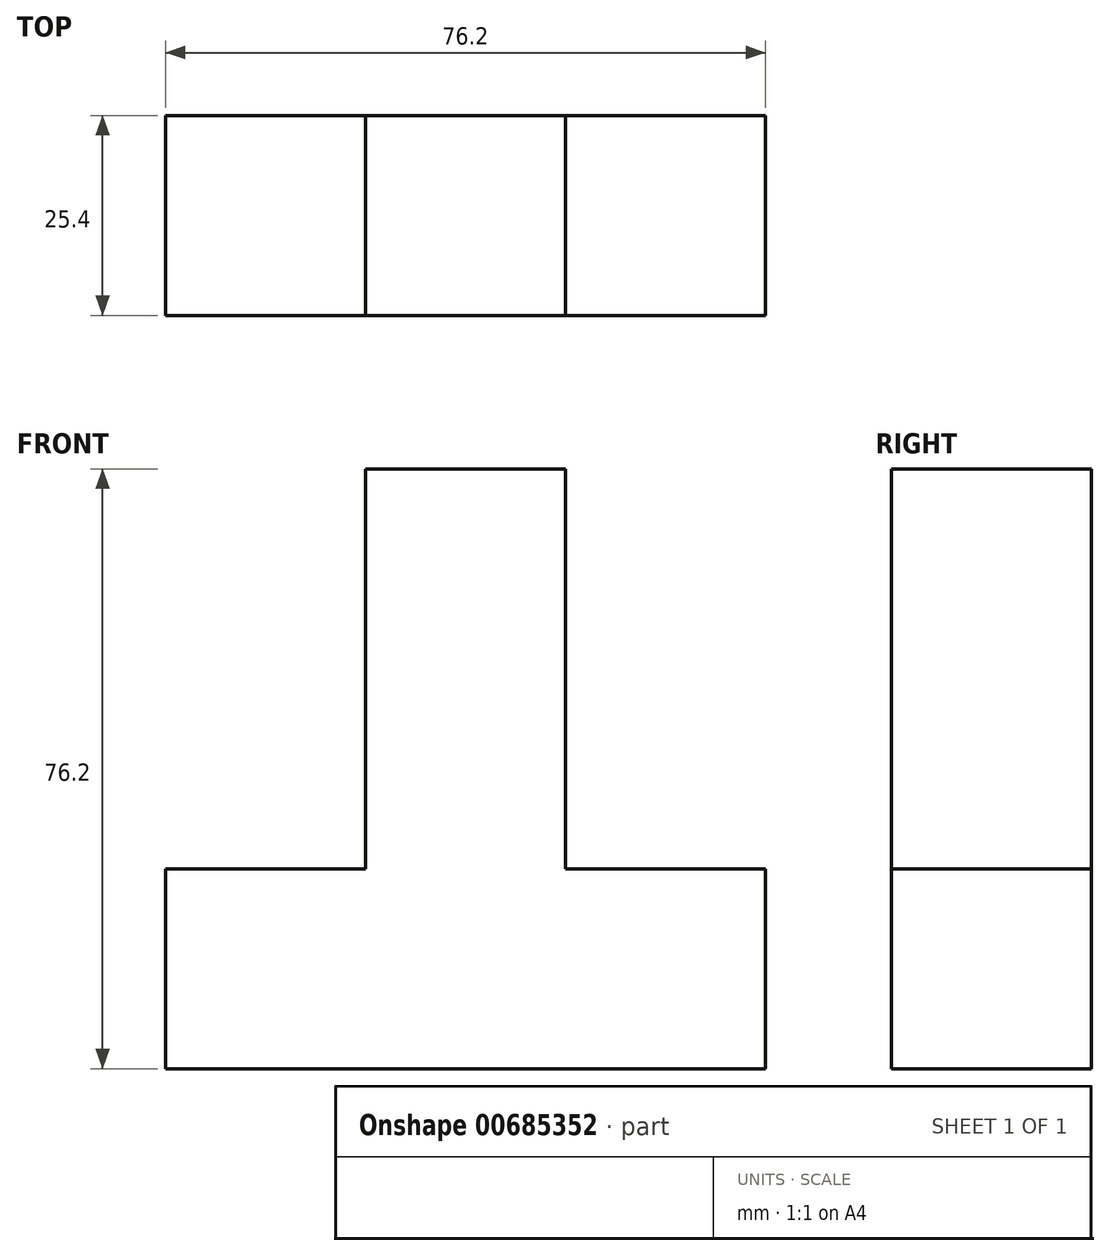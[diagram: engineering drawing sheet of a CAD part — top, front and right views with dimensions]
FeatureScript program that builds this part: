
annotation { "Feature Type Name" : "Feature", "Feature Type Description" : "" }
export const myFeature = defineFeature(function(context is Context, id is Id, definition is map)
    precondition{}
    {
        {
            var Q0;
            Q0=qCreatedBy(makeId("Front.planeOp"),FACE);
            var sketch = newSketch(context, id + "F0", { "sketchPlane" : qUnion([Q0])});
            skLineSegment(sketch, "E0", {"start": v(-40.4, -28.92) * mm, "end": v(35.8, -28.92) * mm});
            skLineSegment(sketch, "E1", {"start": v(-40.4, -28.92) * mm, "end": v(-40.4, -3.52) * mm});
            skLineSegment(sketch, "E2", {"start": v(-40.4, -3.52) * mm, "end": v(-15, -3.52) * mm});
            skLineSegment(sketch, "E3", {"start": v(-15, -3.52) * mm, "end": v(-15, 47.28) * mm});
            skLineSegment(sketch, "E4", {"start": v(35.8, -28.92) * mm, "end": v(35.8, -3.52) * mm});
            skLineSegment(sketch, "E5", {"start": v(35.8, -3.52) * mm, "end": v(10.4, -3.52) * mm});
            skLineSegment(sketch, "E6", {"start": v(10.4, -3.52) * mm, "end": v(10.4, 47.28) * mm});
            skLineSegment(sketch, "E7", {"start": v(-15, 47.28) * mm, "end": v(10.4, 47.28) * mm});
            skSolve(sketch);
        }
        {
            var Q0;
            Q0=makeQuery(id+"F0.imprint","IMPRINT",FACE,{"disambiguationData":[TD([[makeQuery(id+"F0.imprint","IMPRINT",EDGE,{"derivedFrom":sQuery(id+"F0.wireOp",EDGE,"E0")}),1.0]])]});
            extrude(context, id + "F1", {"entities" : qUnion([Q0]), "depth" : 25.4 * mm, "offsetDistance" : 25.4 * mm});
        }
    });
